# Revit family: Pipe-Column
name_source: partatom
category: Structural Columns
revit_build: Autodesk Revit Architecture 2012 (Build: 20110210_1515)
units: mm (PartAtom-declared; Revit-internal decimal feet)

## types (37) — shared parameters
Assembly Code = B10

## per-type parameters (varying)
| type | A | Gauge | ID | OD | W | t |
| Pipe1/2STD | 0.23 in² | Standard | 0' - 0 23/32" | 0' - 0 27/32" | 0.85 | 0' - 0 3/32" |
| Pipe3/4STD | 0.31 in² | Standard | 0' - 0 15/16" | 0' - 1 1/16" | 1.13 | 0' - 0 1/8" |
| Pipe1STD | 0.46 in² | Standard | 0' - 1 3/16" | 0' - 1 5/16" | 1.68 | 0' - 0 1/8" |
| Pipe1-1/4STD | 0.62 in² | Standard | 0' - 1 17/32" | 0' - 1 21/32" | 2.27 | 0' - 0 1/8" |
| Pipe1-1/2STD | 0.75 in² | Standard | 0' - 1 3/4" | 0' - 1 29/32" | 2.72 | 0' - 0 5/32" |
| Pipe2STD | 1 in² | Standard | 0' - 2 7/32" | 0' - 2 3/8" | 3.66 | 0' - 0 5/32" |
| Pipe2-1/2STD | 1.59 in² | Standard | 0' - 2 11/16" | 0' - 2 7/8" | 5.8 | 0' - 0 3/16" |
| Pipe3STD | 2.08 in² | Standard | 0' - 3 9/32" | 0' - 3 1/2" | 7.58 | 0' - 0 7/32" |
| Pipe3-1/2STD | 2.51 in² | Standard | 0' - 3 25/32" | 0' - 4" | 9.12 | 0' - 0 7/32" |
| Pipe4STD | 2.97 in² | Standard | 0' - 4 1/4" | 0' - 4 1/2" | 10.8 | 0' - 0 1/4" |
| Pipe5STD | 4.03 in² | Standard | 0' - 5 5/16" | 0' - 5 9/16" | 14.6 | 0' - 0 1/4" |
| Pipe6STD | 5.22 in² | Standard | 0' - 6 11/32" | 0' - 6 5/8" | 19 | 0' - 0 9/32" |
| Pipe8STD | 7.85 in² | Standard | 0' - 8 5/16" | 0' - 8 5/8" | 28.6 | 0' - 0 5/16" |
| Pipe10STD | 11.1 in² | Standard | 0' - 10 3/8" | 0' - 10 3/4" | 40.5 | 0' - 0 3/8" |
| Pipe12STD | 13.6 in² | Standard | 1' - 0 3/8" | 1' - 0 3/4" | 49.6 | 0' - 0 3/8" |
| Pipe1/2XS | 0.3 in² | X Strong | 0' - 0 11/16" | 0' - 0 27/32" | 1.09 | 0' - 0 5/32" |
| Pipe3/4XS | 0.41 in² | X Strong | 0' - 0 29/32" | 0' - 1 1/16" | 1.48 | 0' - 0 5/32" |
| Pipe1XS | 0.6 in² | X Strong | 0' - 1 1/8" | 0' - 1 5/16" | 2.17 | 0' - 0 3/16" |
| Pipe1-1/4XS | 0.83 in² | X Strong | 0' - 1 15/32" | 0' - 1 21/32" | 3 | 0' - 0 3/16" |
| Pipe1-1/2XS | 1 in² | X Strong | 0' - 1 11/16" | 0' - 1 29/32" | 3.63 | 0' - 0 3/16" |
| Pipe2XS | 1.39 in² | X Strong | 0' - 2 5/32" | 0' - 2 3/8" | 5.03 | 0' - 0 7/32" |
| Pipe2-1/2XS | 2.11 in² | X Strong | 0' - 2 19/32" | 0' - 2 7/8" | 7.67 | 0' - 0 9/32" |
| Pipe3XS | 2.83 in² | X Strong | 0' - 3 3/16" | 0' - 3 1/2" | 10.3 | 0' - 0 5/16" |
| Pipe3-1/2XS | 3.44 in² | X Strong | 0' - 3 11/16" | 0' - 4" | 12.5 | 0' - 0 5/16" |
| Pipe4XS | 4.14 in² | X Strong | 0' - 4 5/32" | 0' - 4 1/2" | 15 | 0' - 0 11/32" |
| Pipe5XS | 5.72 in² | X Strong | 0' - 5 3/16" | 0' - 5 9/16" | 20.8 | 0' - 0 3/8" |
| Pipe6XS | 7.88 in² | X Strong | 0' - 6 3/16" | 0' - 6 5/8" | 28.6 | 0' - 0 7/16" |
| Pipe8XS | 11.9 in² | X Strong | 0' - 8 1/8" | 0' - 8 5/8" | 43.4 | 0' - 0 1/2" |
| Pipe10XS | 15 in² | X Strong | 0' - 10 1/4" | 0' - 10 3/4" | 54.8 | 0' - 0 1/2" |
| Pipe12XS | 17.9 in² | X Strong | 1' - 0 1/4" | 1' - 0 3/4" | 65.5 | 0' - 0 1/2" |
| Pipe2XXS | 2.51 in² | XX Strong | 0' - 1 15/16" | 0' - 2 3/8" | 9.04 | 0' - 0 7/16" |
| Pipe2-1/2XXS | 3.81 in² | XX Strong | 0' - 2 5/16" | 0' - 2 7/8" | 13.7 | 0' - 0 9/16" |
| Pipe3XXS | 5.16 in² | XX Strong | 0' - 2 29/32" | 0' - 3 1/2" | 18.6 | 0' - 0 19/32" |
| Pipe4XXS | 7.64 in² | XX Strong | 0' - 3 13/16" | 0' - 4 1/2" | 27.6 | 0' - 0 11/16" |
| Pipe5XXS | 10.7 in² | XX Strong | 0' - 4 13/16" | 0' - 5 9/16" | 38.6 | 0' - 0 3/4" |
| Pipe6XXS | 14.7 in² | XX Strong | 0' - 5 3/4" | 0' - 6 5/8" | 53.2 | 0' - 0 7/8" |
| Pipe8XXS | 20 in² | XX Strong | 0' - 7 3/4" | 0' - 8 5/8" | 72.5 | 0' - 0 7/8" |

## geometry (parser evidence)
native form markers: Sweep x1
no freeform markers — native parametric forms only
